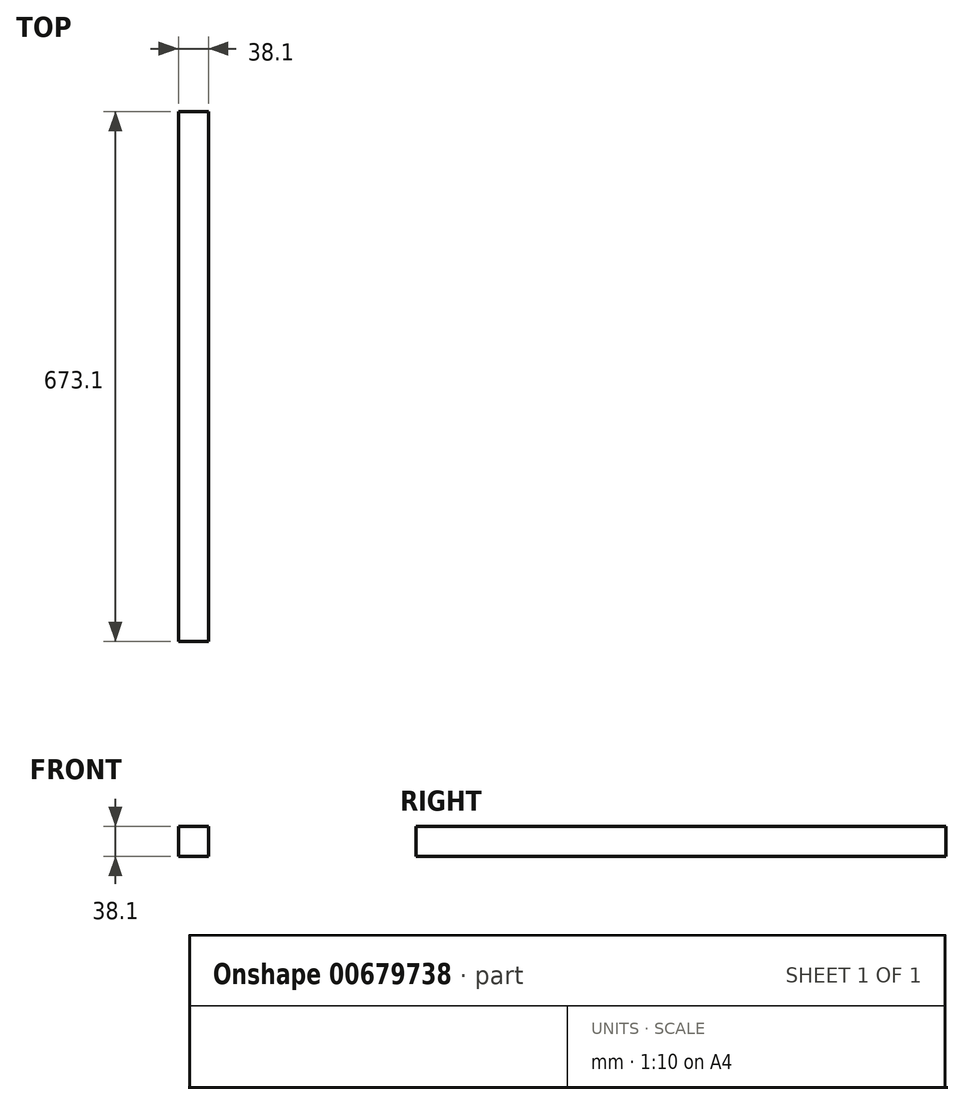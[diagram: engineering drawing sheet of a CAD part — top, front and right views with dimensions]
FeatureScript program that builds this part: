
annotation { "Feature Type Name" : "Feature", "Feature Type Description" : "" }
export const myFeature = defineFeature(function(context is Context, id is Id, definition is map)
    precondition{}
    {
        {
            var Q0;
            Q0=qCreatedBy(makeId("Front.planeOp"),FACE);
            var sketch = newSketch(context, id + "F0", { "sketchPlane" : qUnion([Q0])});
            skLineSegment(sketch, "E0.bottom", {"start": v(19.05, -19.05) * mm, "end": v(-19.05, -19.05) * mm});
            skLineSegment(sketch, "E0.top", {"start": v(19.05, 19.05) * mm, "end": v(-19.05, 19.05) * mm});
            skLineSegment(sketch, "E0.left", {"start": v(19.05, -19.05) * mm, "end": v(19.05, 19.05) * mm});
            skLineSegment(sketch, "E0.right", {"start": v(-19.05, -19.05) * mm, "end": v(-19.05, 19.05) * mm});
            skPoint(sketch, "E0.middle", {"position": v(0, 0) * mm});
            skSolve(sketch);
        }
        {
            var Q0;
            Q0=makeQuery(id+"F0.imprint","IMPRINT",FACE,{"disambiguationData":[TD([[makeQuery(id+"F0.imprint","IMPRINT",EDGE,{"derivedFrom":sQuery(id+"F0.wireOp",EDGE,"E0.bottom")}),-1.0]])]});
            extrude(context, id + "F1", {"entities" : qUnion([Q0]), "endBound" : BoundingType.SYMMETRIC, "depth" : 673.1 * mm, "offsetDistance" : 25.4 * mm});
        }
    });
